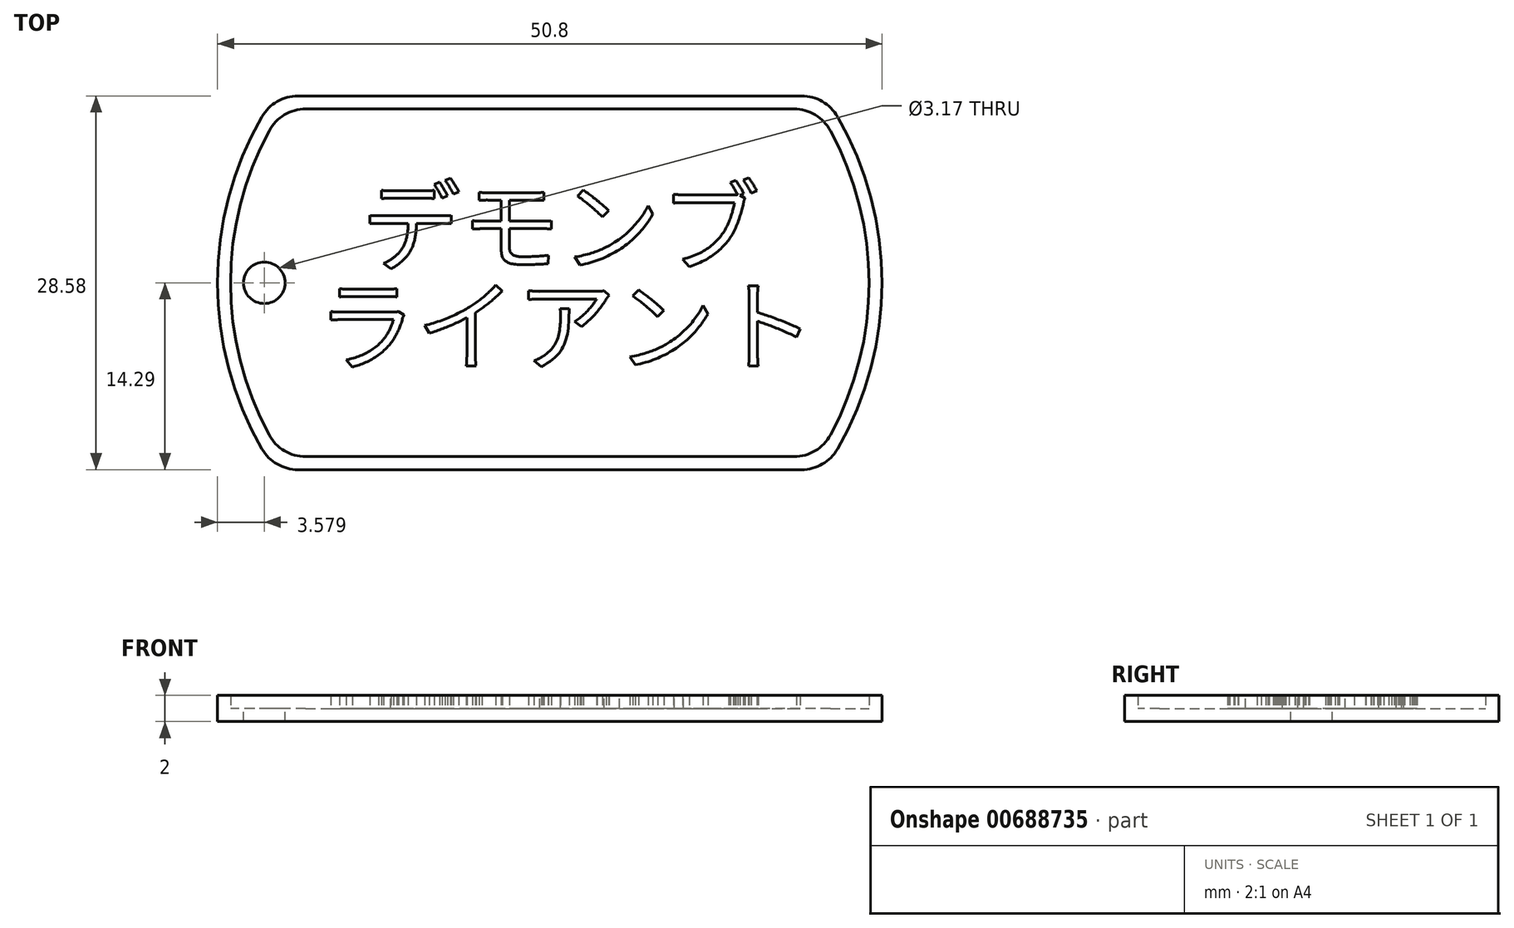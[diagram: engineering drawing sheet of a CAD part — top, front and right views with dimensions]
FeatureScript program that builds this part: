
annotation { "Feature Type Name" : "Feature", "Feature Type Description" : "" }
export const myFeature = defineFeature(function(context is Context, id is Id, definition is map)
    precondition{}
    {
        {
            var Q0;
            Q0=qCreatedBy(makeId("Top.planeOp"),FACE);
            var sketch = newSketch(context, id + "F0", { "sketchPlane" : qUnion([Q0])});
            skArc(sketch, "E0", {"start": v(-22, 12.7) * mm, "mid": v(-25.4, 0) * mm, "end": v(-22, -12.7) * mm});
            skLineSegment(sketch, "E1.top", {"start": v(-19.25, -14.29) * mm, "end": v(19.25, -14.29) * mm});
            skArc(sketch, "E2.trimOffspring", {"start": v(22, -12.7) * mm, "mid": v(25.4, 0) * mm, "end": v(22, 12.7) * mm});
            skLineSegment(sketch, "E3", {"start": v(-19.25, 14.29) * mm, "end": v(19.25, 14.29) * mm});
            skPoint(sketch, "E4.visualSharp", {"position": v(-21, 14.29) * mm});
            skArc(sketch, "E4.filletArc", {"start": v(-19.25, 14.29) * mm, "mid": v(-20.83, 13.86) * mm, "end": v(-22, 12.7) * mm});
            skPoint(sketch, "E5.visualSharp", {"position": v(21, 14.29) * mm});
            skArc(sketch, "E5.filletArc", {"start": v(22, 12.7) * mm, "mid": v(20.83, 13.86) * mm, "end": v(19.25, 14.29) * mm});
            skPoint(sketch, "E6.visualSharp", {"position": v(21, -14.29) * mm});
            skArc(sketch, "E6.filletArc", {"start": v(19.25, -14.29) * mm, "mid": v(20.83, -13.86) * mm, "end": v(22, -12.7) * mm});
            skPoint(sketch, "E7.visualSharp", {"position": v(-21, -14.29) * mm});
            skArc(sketch, "E7.filletArc", {"start": v(-22, -12.7) * mm, "mid": v(-20.83, -13.86) * mm, "end": v(-19.25, -14.29) * mm});
            skSolve(sketch);
        }
        {
            var Q0;
            Q0=makeQuery(id+"F0.imprint","IMPRINT",FACE,{"disambiguationData":[TD([[makeQuery(id+"F0.imprint","IMPRINT",EDGE,{"derivedFrom":sQuery(id+"F0.wireOp",EDGE,"E0")}),1.0]])]});
            extrude(context, id + "F1", {"entities" : qUnion([Q0]), "depth" : 1 * mm, "offsetDistance" : 25.4 * mm});
        }
        {
            var Q0;
            Q0=makeQuery(id+"F1.opExtrude","CAP_FACE",FACE,{"disambiguationData":[OSD([sQuery(id+"F0.wireOp",EDGE,"E0"),sQuery(id+"F0.wireOp",EDGE,"E1.top"),sQuery(id+"F0.wireOp",EDGE,"E2.trimOffspring"),sQuery(id+"F0.wireOp",EDGE,"E3"),sQuery(id+"F0.wireOp",EDGE,"E4.filletArc"),sQuery(id+"F0.wireOp",EDGE,"E5.filletArc"),sQuery(id+"F0.wireOp",EDGE,"E6.filletArc"),sQuery(id+"F0.wireOp",EDGE,"E7.filletArc")])],"isStart":false});
            var sketch = newSketch(context, id + "F2", { "sketchPlane" : qUnion([Q0])});
            skLineSegment(sketch, "E8.0", {"start": v(-18.66, 13.29) * mm, "end": v(18.66, 13.29) * mm});
            skArc(sketch, "E8.1", {"start": v(-21.45, 11.63) * mm, "mid": v(-24.4, 0) * mm, "end": v(-21.45, -11.63) * mm});
            skLineSegment(sketch, "E8.2", {"start": v(-18.66, -13.29) * mm, "end": v(18.66, -13.29) * mm});
            skArc(sketch, "E8.3", {"start": v(21.45, -11.63) * mm, "mid": v(24.4, 0) * mm, "end": v(21.45, 11.63) * mm});
            skPoint(sketch, "E9.visualSharp", {"position": v(-20.46, 13.29) * mm});
            skArc(sketch, "E9.filletArc", {"start": v(-18.66, 13.29) * mm, "mid": v(-20.29, 12.84) * mm, "end": v(-21.45, 11.63) * mm});
            skPoint(sketch, "E10.visualSharp", {"position": v(20.46, 13.29) * mm});
            skArc(sketch, "E10.filletArc", {"start": v(21.45, 11.63) * mm, "mid": v(20.29, 12.84) * mm, "end": v(18.66, 13.29) * mm});
            skPoint(sketch, "E11.visualSharp", {"position": v(20.46, -13.29) * mm});
            skArc(sketch, "E11.filletArc", {"start": v(18.66, -13.29) * mm, "mid": v(20.29, -12.84) * mm, "end": v(21.45, -11.63) * mm});
            skPoint(sketch, "E12.visualSharp", {"position": v(-20.46, -13.29) * mm});
            skArc(sketch, "E12.filletArc", {"start": v(-21.45, -11.63) * mm, "mid": v(-20.29, -12.84) * mm, "end": v(-18.66, -13.29) * mm});
            skLineSegment(sketch, "E13.0", {"start": v(-19.25, 14.29) * mm, "end": v(19.25, 14.29) * mm});
            skArc(sketch, "E13.1", {"start": v(-22, 12.7) * mm, "mid": v(-25.4, 0) * mm, "end": v(-22, -12.7) * mm});
            skLineSegment(sketch, "E13.2", {"start": v(-19.25, -14.29) * mm, "end": v(19.25, -14.29) * mm});
            skArc(sketch, "E13.3", {"start": v(22, -12.7) * mm, "mid": v(25.4, 0) * mm, "end": v(22, 12.7) * mm});
            skPoint(sketch, "E14.visualSharp", {"position": v(-21, -14.29) * mm});
            skArc(sketch, "E14.filletArc", {"start": v(-22, -12.7) * mm, "mid": v(-20.83, -13.86) * mm, "end": v(-19.25, -14.29) * mm});
            skPoint(sketch, "E15.visualSharp", {"position": v(21, -14.29) * mm});
            skArc(sketch, "E15.filletArc", {"start": v(19.25, -14.29) * mm, "mid": v(20.83, -13.86) * mm, "end": v(22, -12.7) * mm});
            skPoint(sketch, "E16.visualSharp", {"position": v(21, 14.29) * mm});
            skArc(sketch, "E16.filletArc", {"start": v(22, 12.7) * mm, "mid": v(20.83, 13.86) * mm, "end": v(19.25, 14.29) * mm});
            skPoint(sketch, "E17.visualSharp", {"position": v(-21, 14.29) * mm});
            skArc(sketch, "E17.filletArc", {"start": v(-19.25, 14.29) * mm, "mid": v(-20.83, 13.86) * mm, "end": v(-22, 12.7) * mm});
            skSolve(sketch);
        }
        {
            var Q0;
            Q0=makeQuery(id+"F2.imprint","IMPRINT",FACE,{"disambiguationData":[TD([[makeQuery(id+"F2.imprint","IMPRINT",EDGE,{"derivedFrom":sQuery(id+"F2.wireOp",EDGE,"E8.0")}),1.0]])]});
            extrude(context, id + "F3", {"entities" : qUnion([Q0]), "operationType" : NewBodyOperationType.ADD, "depth" : 1 * mm, "offsetDistance" : 25.4 * mm});
        }
        {
            var Q0;
            Q0=makeQuery(id+"F1.opExtrude","CAP_FACE",FACE,{"disambiguationData":[OSD([sQuery(id+"F0.wireOp",EDGE,"E0"),sQuery(id+"F0.wireOp",EDGE,"E1.top"),sQuery(id+"F0.wireOp",EDGE,"E2.trimOffspring"),sQuery(id+"F0.wireOp",EDGE,"E3"),sQuery(id+"F0.wireOp",EDGE,"E4.filletArc"),sQuery(id+"F0.wireOp",EDGE,"E5.filletArc"),sQuery(id+"F0.wireOp",EDGE,"E6.filletArc"),sQuery(id+"F0.wireOp",EDGE,"E7.filletArc")])],"isStart":false});
            var sketch = newSketch(context, id + "F4", { "sketchPlane" : qUnion([Q0])});
            skCircle(sketch, "E18", {"center": v(-21.82, 0) * mm, "radius": 1.59 * mm});
            skSolve(sketch);
        }
        {
            var Q0;
            Q0=makeQuery(id+"F4.imprint","IMPRINT",FACE,{"disambiguationData":[TD([[makeQuery(id+"F4.imprint","IMPRINT",EDGE,{"derivedFrom":sQuery(id+"F4.wireOp",EDGE,"E18")}),1.0]])]});
            extrude(context, id + "F5", {"entities" : qUnion([Q0]), "operationType" : NewBodyOperationType.REMOVE, "oppositeDirection" : true, "depth" : 1 * mm, "offsetDistance" : 25.4 * mm});
        }
        {
            var Q0;
            Q0=makeQuery(id+"F1.opExtrude","CAP_FACE",FACE,{"disambiguationData":[OSD([sQuery(id+"F0.wireOp",EDGE,"E0"),sQuery(id+"F0.wireOp",EDGE,"E1.top"),sQuery(id+"F0.wireOp",EDGE,"E2.trimOffspring"),sQuery(id+"F0.wireOp",EDGE,"E3"),sQuery(id+"F0.wireOp",EDGE,"E4.filletArc"),sQuery(id+"F0.wireOp",EDGE,"E5.filletArc"),sQuery(id+"F0.wireOp",EDGE,"E6.filletArc"),sQuery(id+"F0.wireOp",EDGE,"E7.filletArc")])],"isStart":false});
            var sketch = newSketch(context, id + "F6", { "sketchPlane" : qUnion([Q0])});
            skText(sketch, "E19", { "text": "  デモンブ\nライアント", "fontName": "NotoSansCJKjp-Regular.otf"});
            const initialGuessF6  = {"E19": [-0.01783, 0.0015, 1, 0, 0.00549]};
            skSetInitialGuess(sketch, initialGuessF6);
            skSolve(sketch);
        }
        {
            var Q0;
            Q0 = qSketchRegion(id + "F6", true);
            extrude(context, id + "F7", {"entities" : qUnion([Q0]), "operationType" : NewBodyOperationType.ADD, "depth" : 1 * mm, "offsetDistance" : 25.4 * mm});
        }
    });
